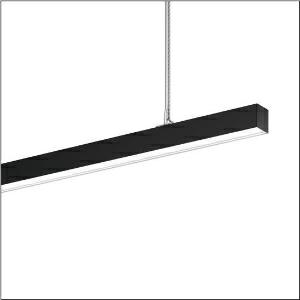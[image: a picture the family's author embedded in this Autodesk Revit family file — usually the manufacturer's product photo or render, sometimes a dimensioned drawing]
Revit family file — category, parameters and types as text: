
# Revit family: silica_r__21_51mx30dc39bb_25b6
name_source: partatom
category: Lighting Fixtures
units: mm (PartAtom-declared; Revit-internal decimal feet)

## family parameters
Cut with Voids When Loaded = No
Host = Face
Light Source = No
Part Type = Normal
Room Calculation Point = No
Round Connector Dimension = Use Diameter
Shared = No

## types (1)
- --- (1 x LED, 10520 lm, 68.3 W, 3000K)
    Apparent Load = 68 VA
    CIE Flux Codes = 47 79 96 57 100
    Color Rendering = 80
    Color Temperature = 3000K
    Default Elevation = 1800 mm
    Description = Silica® 21, office luminaire, primary optical cover: cover, of PMMA, opal, light emission: direct/indirect distribution, primary light characteristic: symmetric, installation type: suspended mounting, LED, rated luminous flux: 10.520lm, luminous efficacy: 154lm/W, light colour: 830, colour temperature: 3000K, with terminal, 3+2-pole, max. 2.5mm², mains connection: 220..240V, AC, 50/60Hz, rated input power: 68.3W, luminaire housing, of aluminium, jet black (RAL 9005), length: 3.004mm, width: 53mm, height: 53mm, protection rating (complete): IP20, insulation class (complete): insulation class I (protective earthing), certification: CE, permissible operating ambient temperature: 0..+35°C, standard: EN 50419, packaging unit: 1 piece
    Height = 53 mm
    Lamp = 1 x LED
    Lamp Light Flux = 10520 lm
    Lamp Power = 68.3 W
    Lamp count = 1
    Length = 3004 mm
    Luminous efficacy = 154 lm/W
    Manufacturer = Siteco
    ModVariant = No
    Model = 51MX30DC39BB
    Mounting Place = Ceiling
    Mounting Type = Pendant
    Number of Poles = 1
    OnlyDefault = Yes
    Power Factor = 1
    Product Name = Silica® 21
    Product group = office luminaire | ceiling pendant
    ProductGroupID = 902
    Protection Class = Protection class I
    Protection Degree = IP 20
    RLX_Detail_Level = 1
    RLX_Emergency_Light_Flux = 0 lm
    RLX_Emergency_Type = 0
    RLX_Emergency_Type_DB = No
    RlxData = <blob elided: 26137 chars, md5=8b84e768>
    Socket = socket
    Standby Power = 0 W
    System Light Flux = 10520 lm
    System Power = 68 W
    Type Comments = factory setting: luminous flux: 100 % | dim-lin: 254 | 233 mA
    Type Image = l_1297744.jpg
    URL = http://relux.com
    VarID = @adj_047265
    Voltage = 0 V
    Weight = 0.00 kg
    Width = 53 mm

## geometry (parser evidence)
native form markers: Blend x4, Sweep x15
no freeform markers — native parametric forms only
